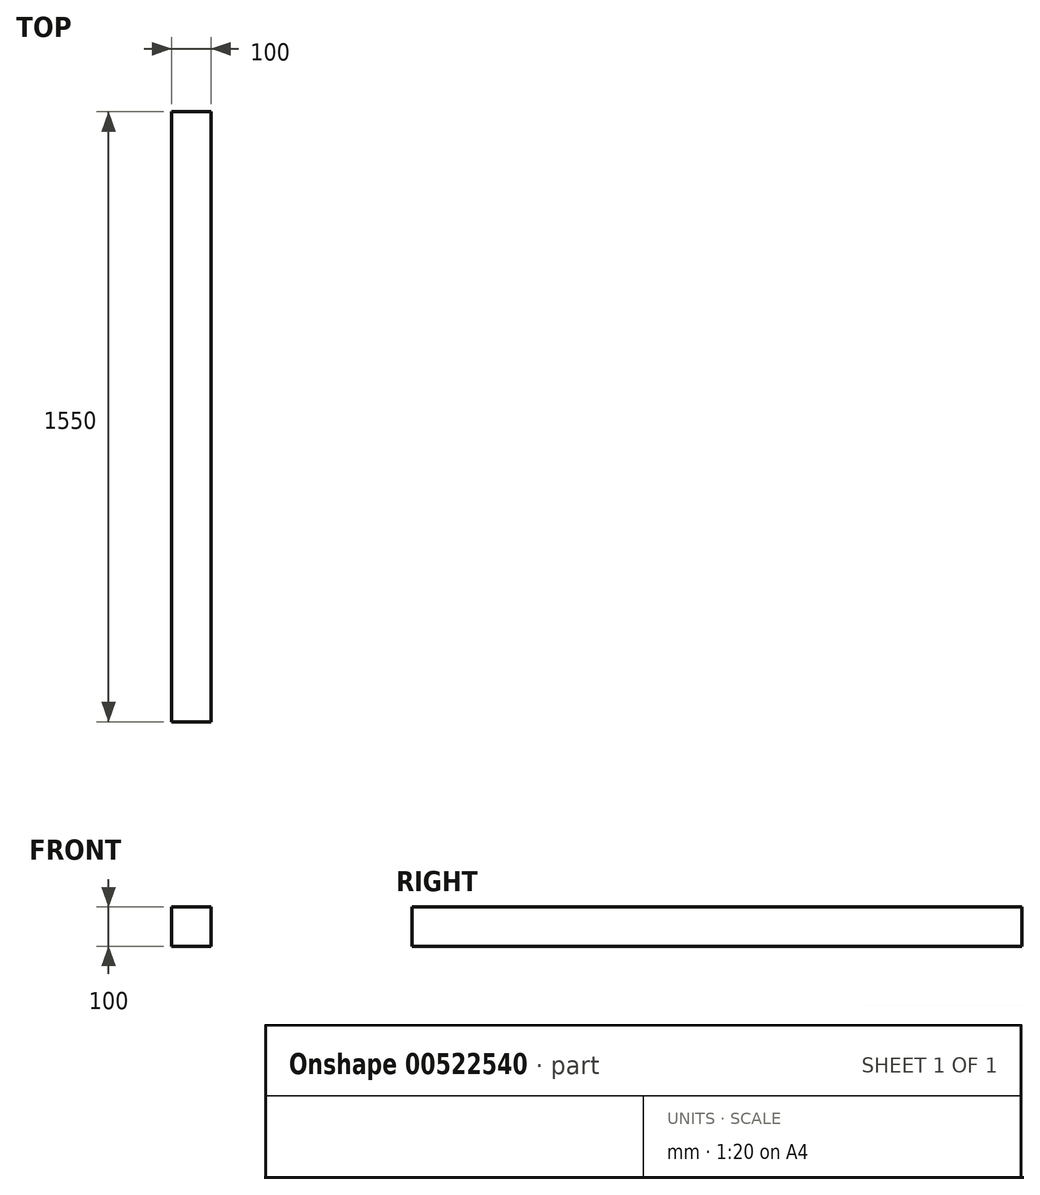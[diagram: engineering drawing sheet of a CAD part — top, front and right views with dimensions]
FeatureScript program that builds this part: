
annotation { "Feature Type Name" : "Feature", "Feature Type Description" : "" }
export const myFeature = defineFeature(function(context is Context, id is Id, definition is map)
    precondition{}
    {
        {
            var Q0;
            Q0=qCreatedBy(makeId("Front.planeOp"),FACE);
            var sketch = newSketch(context, id + "F0", { "sketchPlane" : qUnion([Q0])});
            skLineSegment(sketch, "E0.bottom", {"start": v(-118.75, 94.8) * mm, "end": v(-18.75, 94.8) * mm});
            skLineSegment(sketch, "E0.top", {"start": v(-118.75, -5.2) * mm, "end": v(-18.75, -5.2) * mm});
            skLineSegment(sketch, "E0.left", {"start": v(-118.75, 94.8) * mm, "end": v(-118.75, -5.2) * mm});
            skLineSegment(sketch, "E0.right", {"start": v(-18.75, 94.8) * mm, "end": v(-18.75, -5.2) * mm});
            skSolve(sketch);
        }
        {
            var Q0;
            Q0=qSketchRegion(id+"F0",true);
            extrude(context, id + "F1", {"entities" : qUnion([Q0]), "depth" : 1550 * mm, "offsetDistance" : 25 * mm});
        }
    });
